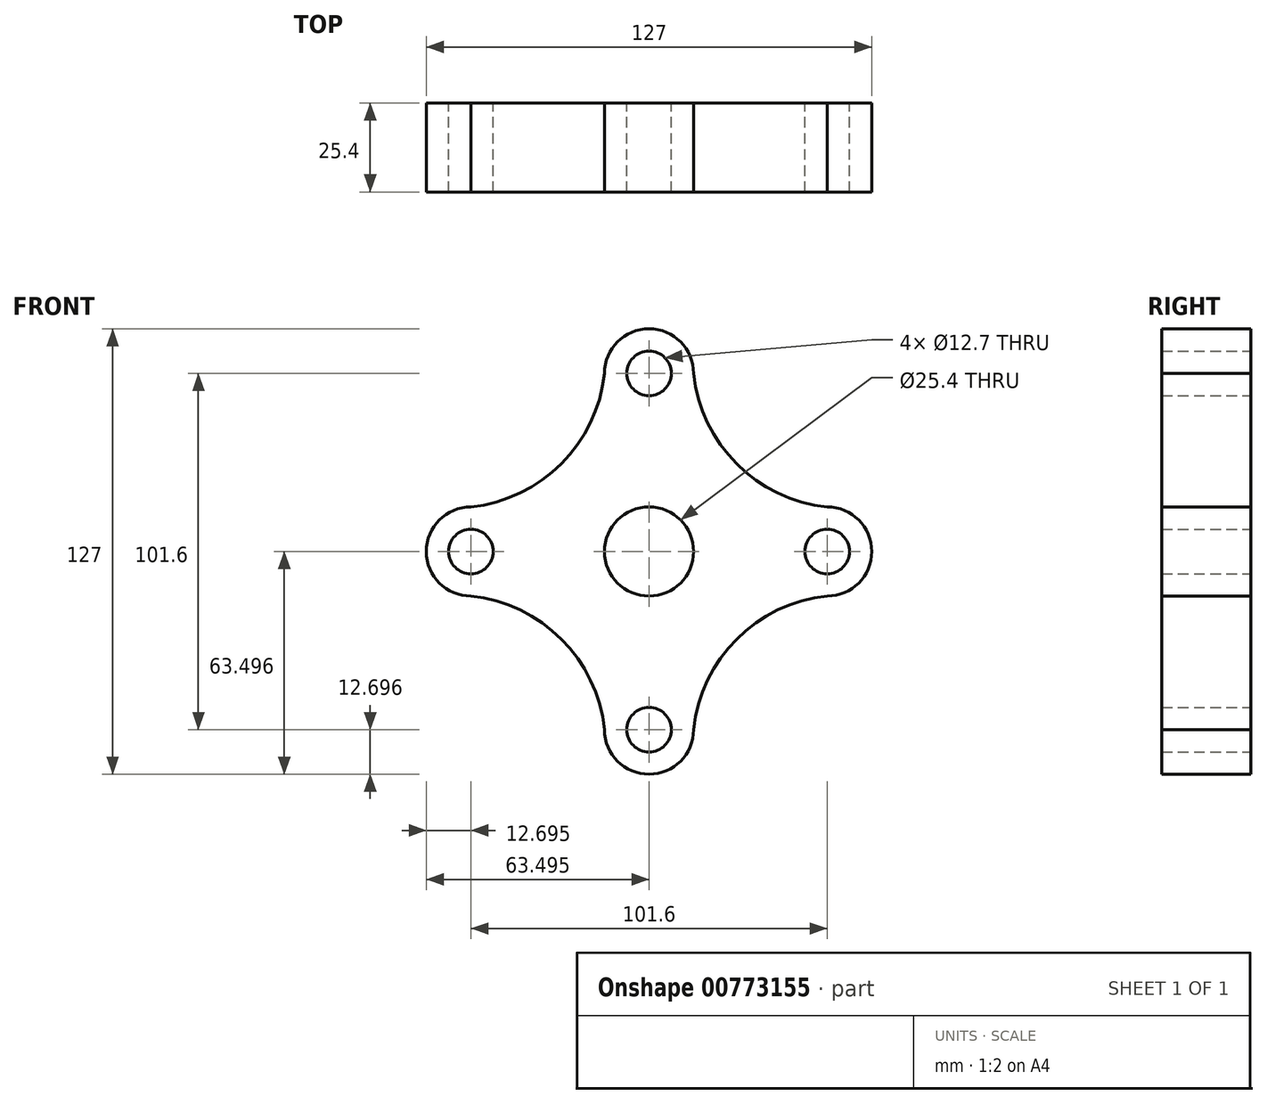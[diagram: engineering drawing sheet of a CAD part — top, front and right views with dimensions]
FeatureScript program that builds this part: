
annotation { "Feature Type Name" : "Feature", "Feature Type Description" : "" }
export const myFeature = defineFeature(function(context is Context, id is Id, definition is map)
    precondition{}
    {
        {
            var Q0;
            Q0=qCreatedBy(makeId("Front.planeOp"),FACE);
            var sketch = newSketch(context, id + "F0", { "sketchPlane" : qUnion([Q0])});
            skCircle(sketch, "E0", {"center": v(-51.08, 0.48) * mm, "radius": 6.35 * mm});
            skCircle(sketch, "E1", {"center": v(50.52, 0.48) * mm, "radius": 6.35 * mm});
            skCircle(sketch, "E2", {"center": v(-0.28, 0.48) * mm, "radius": 12.7 * mm});
            skCircle(sketch, "E3", {"center": v(-0.28, -50.32) * mm, "radius": 6.35 * mm});
            skCircle(sketch, "E4", {"center": v(-0.28, 51.28) * mm, "radius": 6.35 * mm});
            skArc(sketch, "E5", {"start": v(-51.08, 13.18) * mm, "mid": v(-25.31, 25.5) * mm, "end": v(-12.98, 51.28) * mm});
            skArc(sketch, "E6", {"start": v(12.42, 51.28) * mm, "mid": v(-0.28, 63.98) * mm, "end": v(-12.98, 51.28) * mm});
            skArc(sketch, "E7", {"start": v(-51.08, 13.18) * mm, "mid": v(-63.78, 0.48) * mm, "end": v(-51.08, -12.22) * mm});
            skPoint(sketch, "E8.trimOffspring.end.orphan", {"position": v(-51.08, 51.28) * mm});
            skArc(sketch, "E9", {"start": v(12.42, 51.28) * mm, "mid": v(24.7, 25.46) * mm, "end": v(50.52, 13.18) * mm});
            skArc(sketch, "E10", {"start": v(50.52, -12.22) * mm, "mid": v(63.22, 0.48) * mm, "end": v(50.52, 13.18) * mm});
            skPoint(sketch, "E11.orphan", {"position": v(50.52, 51.28) * mm});
            skArc(sketch, "E12", {"start": v(50.52, -12.22) * mm, "mid": v(24.7, -24.5) * mm, "end": v(12.42, -50.32) * mm});
            skArc(sketch, "E13", {"start": v(-12.98, -50.32) * mm, "mid": v(-0.28, -63.02) * mm, "end": v(12.42, -50.32) * mm});
            skArc(sketch, "E14", {"start": v(-12.98, -50.32) * mm, "mid": v(-25.27, -24.5) * mm, "end": v(-51.08, -12.22) * mm});
            skPoint(sketch, "E15.orphan", {"position": v(-51.08, -50.32) * mm});
            skPoint(sketch, "E16.orphan", {"position": v(50.52, -50.32) * mm});
            skSolve(sketch);
        }
        {
            var Q0;
            Q0 = qSketchRegion(id + "F0", true);
            extrude(context, id + "F1", {"entities" : qUnion([Q0]), "depth" : 25.4 * mm, "offsetDistance" : 25.4 * mm});
        }
    });
